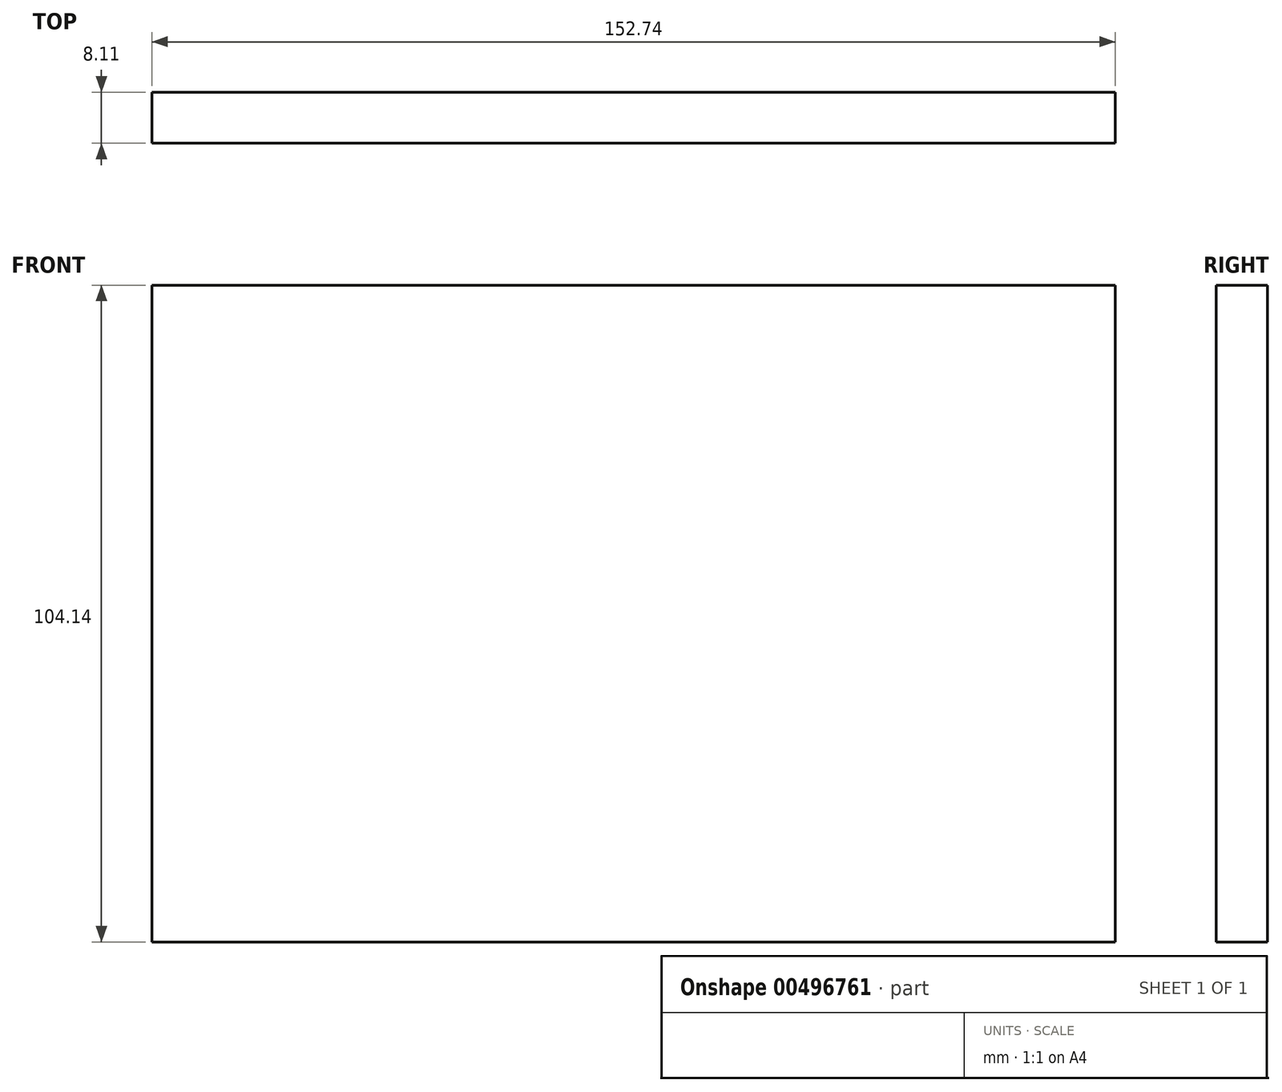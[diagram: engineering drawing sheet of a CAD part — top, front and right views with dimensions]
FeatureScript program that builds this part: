
annotation { "Feature Type Name" : "Feature", "Feature Type Description" : "" }
export const myFeature = defineFeature(function(context is Context, id is Id, definition is map)
    precondition{}
    {
        {
            var Q0;
            Q0=qCreatedBy(makeId("Top.planeOp"),FACE);
            var sketch = newSketch(context, id + "F0", { "sketchPlane" : qUnion([Q0])});
            skLineSegment(sketch, "E0", {"start": v(-76.65, 0) * mm, "end": v(-76.65, 8.11) * mm});
            skLineSegment(sketch, "E1", {"start": v(-76.65, 8.11) * mm, "end": v(76.1, 8.11) * mm});
            skLineSegment(sketch, "E2", {"start": v(76.1, 8.11) * mm, "end": v(76.1, 0) * mm});
            skLineSegment(sketch, "E3", {"start": v(76.1, 0) * mm, "end": v(-76.65, 0) * mm});
            skSolve(sketch);
        }
        {
            var Q0;
            Q0=makeQuery(id+"F0.imprint","IMPRINT",FACE,{"disambiguationData":[TD([[makeQuery(id+"F0.imprint","IMPRINT",EDGE,{"derivedFrom":sQuery(id+"F0.wireOp",EDGE,"E0")}),-1.0]])]});
            extrude(context, id + "F1", {"entities" : qUnion([Q0]), "depth" : 104.14 * mm});
        }
    });
